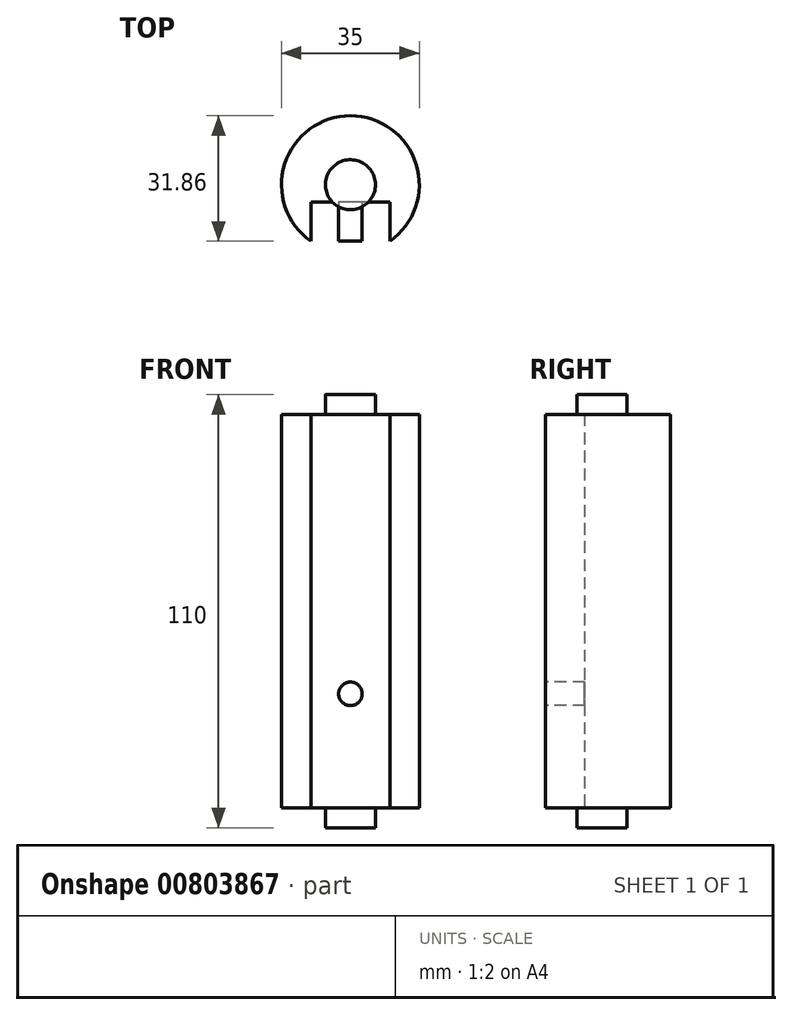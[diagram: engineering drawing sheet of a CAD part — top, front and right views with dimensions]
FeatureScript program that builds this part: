
annotation { "Feature Type Name" : "Feature", "Feature Type Description" : "" }
export const myFeature = defineFeature(function(context is Context, id is Id, definition is map)
    precondition{}
    {
        {
            var Q0;
            Q0=qCreatedBy(makeId("Top.planeOp"),FACE);
            var sketch = newSketch(context, id + "F0", { "sketchPlane" : qUnion([Q0])});
            skCircle(sketch, "E0", {"center": v(0, 0) * mm, "radius": 17.5 * mm});
            skCircle(sketch, "E1", {"center": v(0, 0) * mm, "radius": 6.35 * mm});
            skLineSegment(sketch, "E2", {"start": v(10, -14.36) * mm, "end": v(-10, -14.36) * mm});
            skSolve(sketch);
        }
        {
            var Q0;
            Q0=makeQuery(id+"F0.imprint","IMPRINT",FACE,{"disambiguationData":[TD([[makeQuery(id+"F0.imprint","IMPRINT",EDGE,{"derivedFrom":sQuery(id+"F0.wireOp",EDGE,"E1")}),-1.0]])]});
            var Q1;
            Q1=makeQuery(id+"F0.imprint","IMPRINT",FACE,{"disambiguationData":[TD([[makeQuery(id+"F0.imprint","IMPRINT",EDGE,{"derivedFrom":sQuery(id+"F0.wireOp",EDGE,"E1")}),1.0]])]});
            extrude(context, id + "F1", {"entities" : qUnion([Q0, Q1]), "endBound" : BoundingType.SYMMETRIC, "depth" : 100 * mm, "offsetDistance" : 25 * mm});
        }
        {
            var Q0;
            Q0=makeQuery(id+"F0.imprint","IMPRINT",FACE,{"disambiguationData":[TD([[makeQuery(id+"F0.imprint","IMPRINT",EDGE,{"derivedFrom":sQuery(id+"F0.wireOp",EDGE,"E1")}),1.0]])]});
            extrude(context, id + "F2", {"entities" : qUnion([Q0]), "operationType" : NewBodyOperationType.ADD, "endBound" : BoundingType.SYMMETRIC, "depth" : 110 * mm, "offsetDistance" : 25 * mm});
        }
        {
            var Q0;
            Q0=makeQuery(id+"F1.opExtrude","SWEPT_FACE",FACE,{"disambiguationData":[OSD([sQuery(id+"F0.wireOp",EDGE,"E2")])]});
            var sketch = newSketch(context, id + "F3", { "sketchPlane" : qUnion([Q0])});
            skCircle(sketch, "E3", {"center": v(0, 21) * mm, "radius": 3 * mm});
            skCircle(sketch, "E4.MirrorC", {"center": v(0, -21) * mm, "radius": 3 * mm});
            skSolve(sketch);
        }
        {
            var Q0;
            Q0=makeQuery(id+"F3.imprint","IMPRINT",FACE,{"disambiguationData":[TD([[makeQuery(id+"F3.imprint","IMPRINT",EDGE,{"derivedFrom":sQuery(id+"F3.wireOp",EDGE,"E3")}),1.0]])]});
            var Q1;
            Q1=makeQuery(id+"F3.imprint","IMPRINT",FACE,{"disambiguationData":[TD([[makeQuery(id+"F3.imprint","IMPRINT",EDGE,{"derivedFrom":sQuery(id+"F3.wireOp",EDGE,"E4.MirrorC")}),-1.0]])]});
            extrude(context, id + "F4", {"entities" : qUnion([Q0, Q1]), "operationType" : NewBodyOperationType.REMOVE, "oppositeDirection" : true, "depth" : 10 * mm, "offsetDistance" : 25 * mm});
        }
    });
